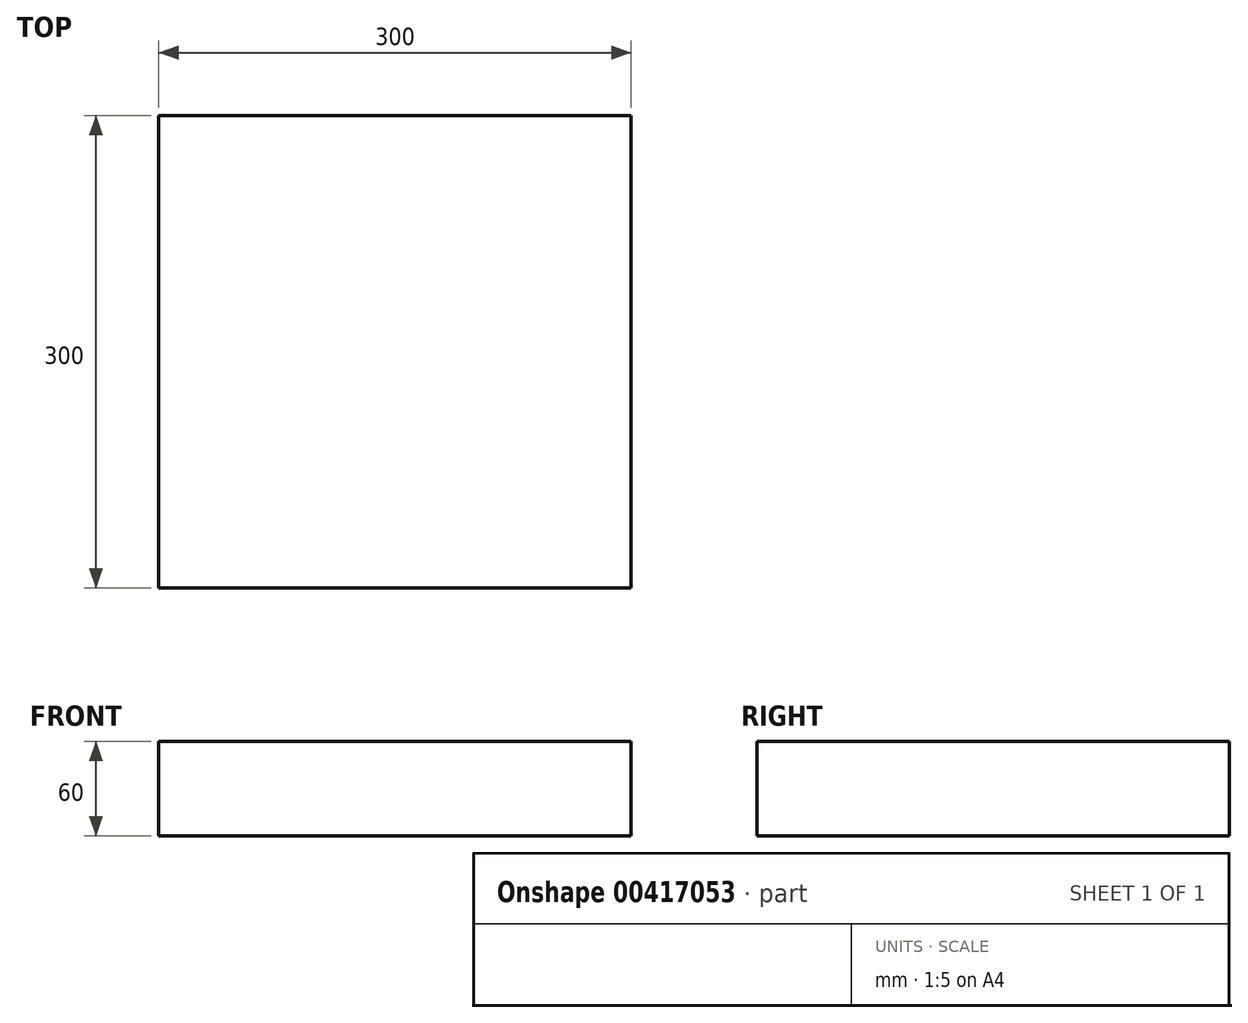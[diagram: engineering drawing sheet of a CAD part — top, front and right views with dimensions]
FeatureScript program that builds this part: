
annotation { "Feature Type Name" : "Feature", "Feature Type Description" : "" }
export const myFeature = defineFeature(function(context is Context, id is Id, definition is map)
    precondition{}
    {
        {
            var Q0;
            Q0=qCreatedBy(makeId("Front.planeOp"),FACE);
            var sketch = newSketch(context, id + "F0", { "sketchPlane" : qUnion([Q0])});
            skLineSegment(sketch, "E0", {"start": v(150, 0) * mm, "end": v(150, 30) * mm});
            skLineSegment(sketch, "E1", {"start": v(150, 30) * mm, "end": v(-150, 30) * mm});
            skLineSegment(sketch, "E2", {"start": v(150, 0) * mm, "end": v(150, -30) * mm});
            skLineSegment(sketch, "E3", {"start": v(150, -30) * mm, "end": v(-150, -30) * mm});
            skLineSegment(sketch, "E4", {"start": v(-150, 30) * mm, "end": v(-150, -30) * mm});
            skSolve(sketch);
        }
        {
            var Q0;
            Q0=makeQuery(id+"F0.imprint","IMPRINT",FACE,{"disambiguationData":[TD([[makeQuery(id+"F0.imprint","IMPRINT",EDGE,{"derivedFrom":sQuery(id+"F0.wireOp",EDGE,"E0")}),1.0]])]});
            extrude(context, id + "F1", {"entities" : qUnion([Q0]), "depth" : 300 * mm, "offsetDistance" : 25 * mm});
        }
    });
